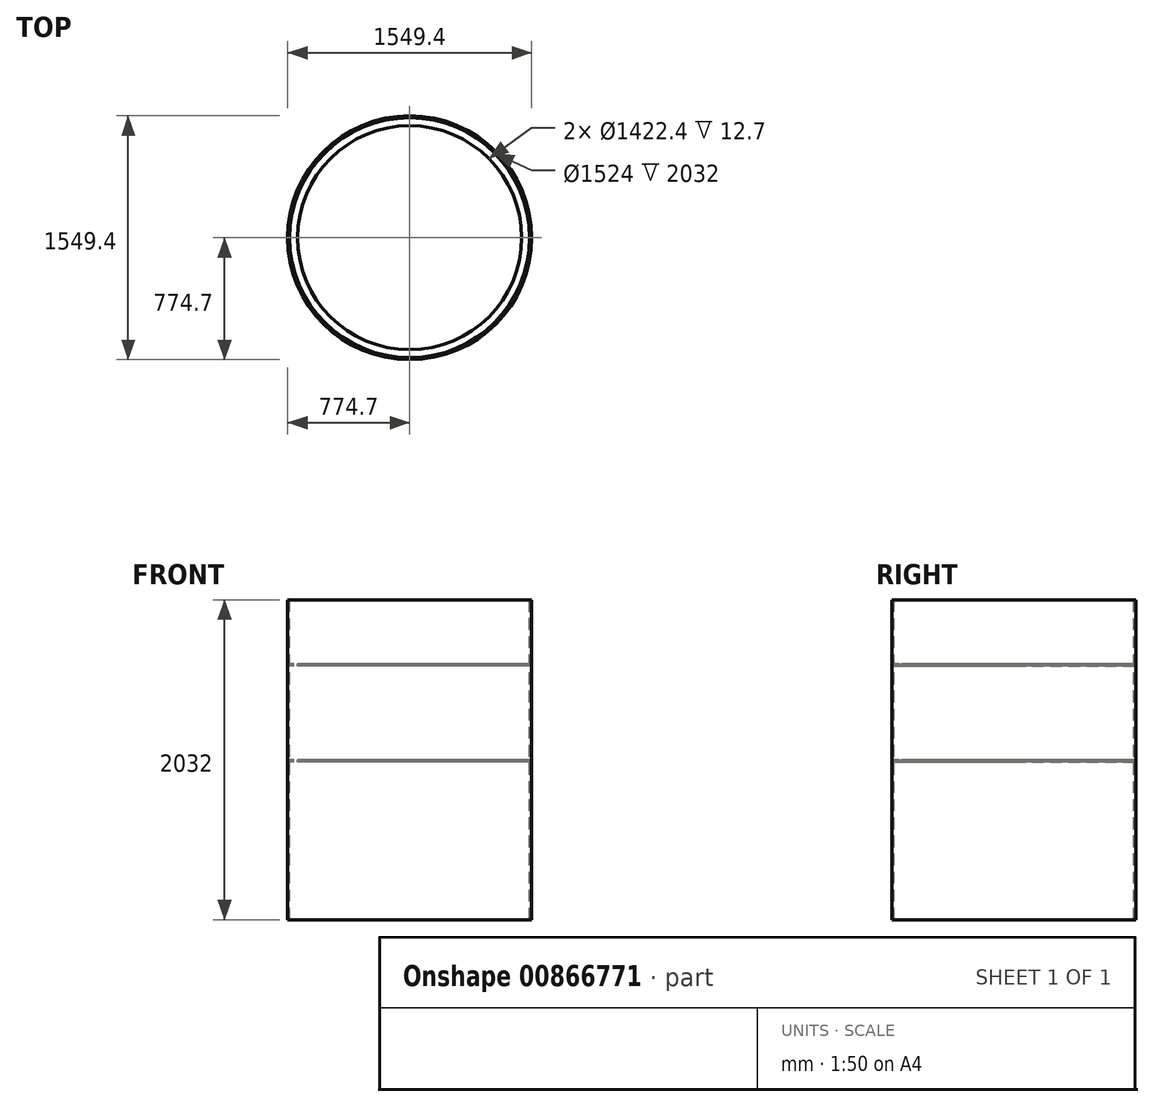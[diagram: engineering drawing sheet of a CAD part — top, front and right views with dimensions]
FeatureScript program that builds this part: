
annotation { "Feature Type Name" : "Feature", "Feature Type Description" : "" }
export const myFeature = defineFeature(function(context is Context, id is Id, definition is map)
    precondition{}
    {
        {
            var Q0;
            Q0=qCreatedBy(makeId("Top.planeOp"),FACE);
            var sketch = newSketch(context, id + "F0", { "sketchPlane" : qUnion([Q0])});
            skCircle(sketch, "E0", {"center": v(0, 0) * mm, "radius": 762 * mm});
            skCircle(sketch, "E1", {"center": v(0, 0) * mm, "radius": 711.2 * mm});
            skCircle(sketch, "E2", {"center": v(0, 0) * mm, "radius": 774.7 * mm});
            skSolve(sketch);
        }
        {
            var Q0;
            Q0=makeQuery(id+"F0.imprint","IMPRINT",FACE,{"disambiguationData":[TD([[makeQuery(id+"F0.imprint","IMPRINT",EDGE,{"derivedFrom":sQuery(id+"F0.wireOp",EDGE,"E0")}),1.0]])]});
            extrude(context, id + "F1", {"entities" : qUnion([Q0]), "oppositeDirection" : true, "depth" : 12.7 * mm, "offsetDistance" : 25.4 * mm});
        }
        {
            var Q0;
            Q0=makeQuery(id+"F0.imprint","IMPRINT",FACE,{"disambiguationData":[TD([[makeQuery(id+"F0.imprint","IMPRINT",EDGE,{"derivedFrom":sQuery(id+"F0.wireOp",EDGE,"E0")}),-1.0]])]});
            extrude(context, id + "F2", {"entities" : qUnion([Q0]), "oppositeDirection" : true, "depth" : 2032 * mm, "offsetDistance" : 25.4 * mm, "symmetric" : true});
        }
        {
            var Q0;
            Q0=qCreatedBy(makeId("Top.planeOp"),FACE);
            cPlane(context, id + "F3", {"entities" : qUnion([Q0]), "cplaneType" : CPlaneType.OFFSET, "offset" : 609.6 * mm, "width" : 152.4 * mm, "height" : 152.4 * mm});
        }
        {
            var Q0;
            Q0=qCreatedBy(id+"F3.planeOp",FACE);
            var sketch = newSketch(context, id + "F4", { "sketchPlane" : qUnion([Q0])});
            skCircle(sketch, "E3", {"center": v(0, 0) * mm, "radius": 762 * mm});
            skCircle(sketch, "E4", {"center": v(0, 0) * mm, "radius": 711.2 * mm});
            skSolve(sketch);
        }
        {
            var Q0;
            Q0=makeQuery(id+"F4.imprint","IMPRINT",FACE,{"disambiguationData":[TD([[makeQuery(id+"F4.imprint","IMPRINT",EDGE,{"derivedFrom":sQuery(id+"F4.wireOp",EDGE,"E3")}),1.0]])]});
            extrude(context, id + "F5", {"entities" : qUnion([Q0]), "oppositeDirection" : true, "depth" : 12.7 * mm, "offsetDistance" : 25.4 * mm});
        }
    });
